# Revit family: ПТУ_общий фундамент
name_source: partatom
category: Специальное оборудование
units: mm (PartAtom-declared; Revit-internal decimal feet)

## family parameters
Всегда вертикально = Нет
На основе рабочей плоскости = Нет
Общий = Нет
При загрузке вырезать с полостями = Нет
Размер круглого соединителя = Использовать диаметр
Тип детали = Нормальный
Точка расчета площади = Нет

## types (8) — shared parameters
ADSK_Единица измерения = шт.
ADSK_Завод-изготовитель = FENSYS
ADSK_Комплект = ПТУ
URL = https://www.fensys.ru

## per-type parameters (varying)
| type | ADSK_Код изделия | ADSK_Масса | ADSK_Наименование | ADSK_Обозначение | Длина стрелы | Объём бетона | Объём вынимаего грунта |
| ПТУ с общим фундаментом., под 6000.,Тёплое исполнение | 53439 | 2500 | Противотаранное устройство с вертикальным подъемом стрелы для остановки т/с массой 3,5 т на скорости 40 км/ч. Перекрываемый проезд 6 м. Электромеханический привод. В комплекте с армокаркасом для монолитного фундамента. Высота стрелы над дорогой - 860 мм. Время закрывания 12 с. Потр. мощность 3 кВт. Температура эксплуатации -20°-+50°. В комплекте: ШУ, пост управления, ф/э безопасности, маячок. | ПТУ-Л 6000ТМ | 6000 мм | 8.9 | 9 |
| ПТУ с общим фундаментом., под 6000.,Холодное исполнение | 53435 | 2500 | Противотаранное устройство с вертикальным подъемом стрелы для остановки т/с массой 3,5 т на скорости 40 км/ч. Перекрываемый проезд 6 м. Электромеханический привод. В комплекте с армокаркасом для монолитного фундамента. Высота стрелы над дорогой - 860 мм. Время закрывания 12 с. Потр.мощность 5 кВт. Температура эксплуатации -55°-+50°. В комплекте: ШУ, пост управления, ф/э безопасности, маячок. | ПТУ-Л 6000ХМ | 6000 мм | 8.9 | 9 |
| ПТУ с общим фундаментом., под 4000.,Тёплое исполнение | 53436 | 2200 | Противотаранное устройство с вертикальным подъемом стрелы для остановки т/с массой 3,5 т на скорости 40 км/ч. Перекрываемый проезд 4 м. Электромеханический привод. В комплекте с армокаркасом для монолитного фундамента. Высота стрелы над дорогой - 860 мм. Время закрывания 12 с. Потр. мощность 3 кВт. Температура эксплуатации -20°-+50°. В комплекте: ШУ, пост управления, ф/э безопасности, маячок. | ПТУ-Л 4000ТМ | 4000 мм | 5.7 | 5.8 |
| ПТУ с общим фундаментом., под 4000.,Холодное исполнение | 53432 | 2200 | Противотаранное устройство с вертикальным подъемом стрелы для остановки т/с массой 3,5 т на скорости 40 км/ч. Перекрываемый проезд 4 м. Электромеханический привод. В комплекте с армокаркасом для монолитного фундамента. Высота стрелы над дорогой - 860 мм. Время закрывания 12 с. Потр.мощность 5 кВт. Температура эксплуатации -55°-+50°. В комплекте: ШУ, пост управления, ф/э безопасности, маячок. | ПТУ-Л 4000ХМ | 4000 мм | 5.7 | 5.8 |
| ПТУ с общим фундаментом., под 4500.,Тёплое исполнение | 53437 | 2280 | Противотаранное устройство с вертикальным подъемом стрелы для остановки т/с массой 3,5 т на скорости 40 км/ч. Перекрываемый проезд 4,5 м. Электромеханический привод. В комплекте с армокаркасом для монолитного фундамента. Высота стрелы над дорогой - 860 мм. Время закрывания 12 с. Потр. мощность 3 кВт. Температура эксплуатации -20°-+50°. В комплекте: ШУ, пост управления, ф/э безопасности, маячок. | ПТУ-Л 4500ТМ | 4500 мм | 7.3 | 7.4 |
| ПТУ с общим фундаментом., под 4500.,Холодное исполнение | 53433 | 2250 | Противотаранное устройство с вертикальным подъемом стрелы для остановки т/с массой 3,5 т на скорости 40 км/ч. Перекрываемый проезд 4,5 м. Электромеханический привод. В комплекте с армокаркасом для монолитного фундамента. Высота стрелы над дорогой - 860 мм. Время закрывания 12 с. Потр.мощность 5 кВт. Температура эксплуатации -55°-+50°. В комплекте: ШУ, пост управления, ф/э безопасности, маячок. | ПТУ-Л 4500ХМ | 4500 мм | 7.3 | 7.4 |
| ПТУ с общим фундаментом., под 5000.,Холодное исполнение | 53434 | 2350 | Противотаранное устройство с вертикальным подъемом стрелы для остановки т/с массой 3,5 т на скорости 40 км/ч. Перекрываемый проезд 5 м. Электромеханический привод. В комплекте с армокаркасом для монолитного фундамента. Высота стрелы над дорогой - 860 мм. Время закрывания 12 с. Потр.мощность 5 кВт. Температура эксплуатации -55°-+50°. В комплекте: ШУ, пост управления,ф/э безопасности, маячок. | ПТУ-Л 5000ХМ | 5000 мм | 7.8 | 7.9 |
| ПТУ с общим фундаментом., под 5000.,Тёплое исполнение | 53438 | 2350 | Противотаранное устройство с вертикальным подъемом стрелы для остановки т/с массой 3,5 т на скорости 40 км/ч. Перекрываемый проезд 5 м. Электромеханический привод. В комплекте с армокаркасом для монолитного фундамента. Высота стрелы над дорогой - 860 мм. Время закрывания 12 с. Потр. мощность 3 кВт. Температура эксплуатации -20°-+50°. В комплекте: ШУ, пост управления,ф/э безопасности, маячок. | ПТУ-Л 5000ТМ | 5000 мм | 7.8 | 7.9 |
